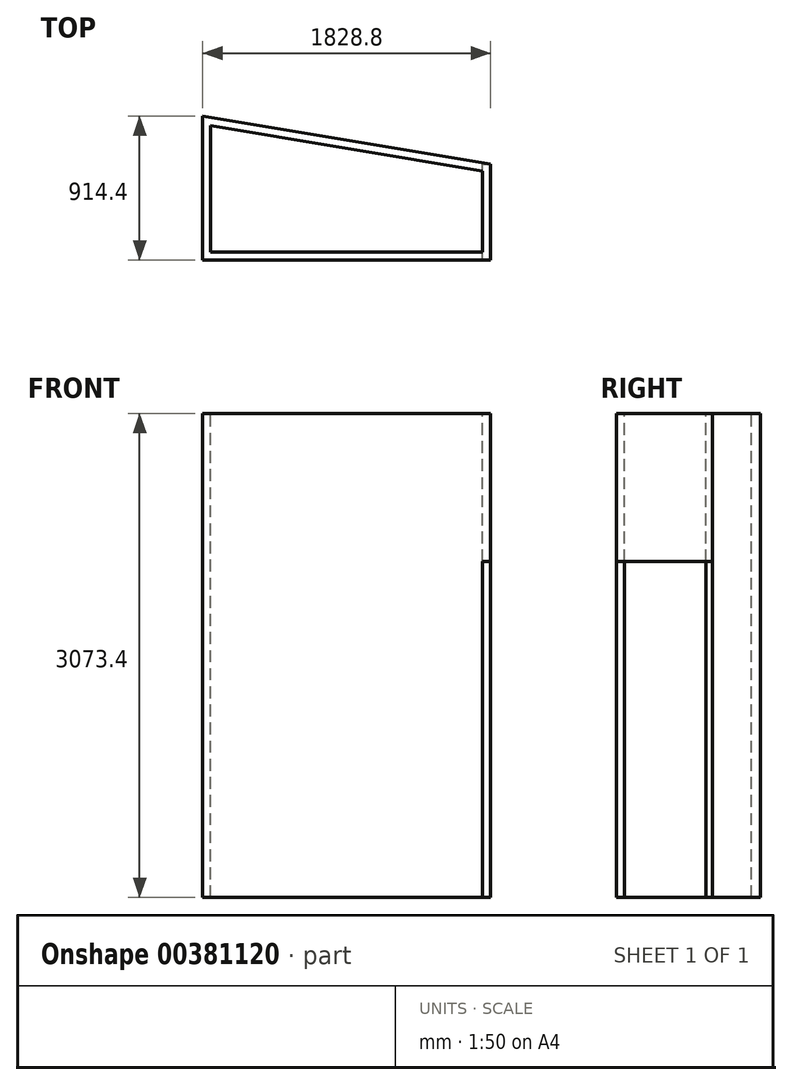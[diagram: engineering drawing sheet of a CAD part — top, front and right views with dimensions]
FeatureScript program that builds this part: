
annotation { "Feature Type Name" : "Feature", "Feature Type Description" : "" }
export const myFeature = defineFeature(function(context is Context, id is Id, definition is map)
    precondition{}
    {
        {
            var Q0;
            Q0=qCreatedBy(makeId("Top.planeOp"),FACE);
            var sketch = newSketch(context, id + "F0", { "sketchPlane" : qUnion([Q0])});
            skSolve(sketch);
        }
        {
            var Q0;
            Q0=qCreatedBy(makeId("Top.planeOp"),FACE);
            var sketch = newSketch(context, id + "F1", { "sketchPlane" : qUnion([Q0])});
            skLineSegment(sketch, "E0", {"start": v(-931.25, -130.48) * mm, "end": v(897.55, -130.48) * mm});
            skLineSegment(sketch, "E1", {"start": v(-931.25, -130.48) * mm, "end": v(-931.25, 783.92) * mm});
            skLineSegment(sketch, "E2", {"start": v(897.55, -130.48) * mm, "end": v(897.55, 479.12) * mm});
            skLineSegment(sketch, "E3", {"start": v(-931.25, 783.92) * mm, "end": v(897.55, 479.12) * mm});
            skSolve(sketch);
        }
        {
            var Q0;
            Q0=qSketchRegion(id+"F0",true);
            var Q1;
            Q1=makeQuery(id+"F1.imprint","IMPRINT",FACE,{"disambiguationData":[TD([[makeQuery(id+"F1.imprint","IMPRINT",EDGE,{"derivedFrom":sQuery(id+"F1.wireOp",EDGE,"E0")}),1.0]])]});
            extrude(context, id + "F2", {"entities" : qUnion([Q0, Q1]), "depth" : 25.4 * mm});
        }
        {
            var Q0;
            Q0=makeQuery(id+"F2.opExtrude","CAP_FACE",FACE,{"disambiguationData":[OSD([sQuery(id+"F1.wireOp",EDGE,"E0"),sQuery(id+"F1.wireOp",EDGE,"E1"),sQuery(id+"F1.wireOp",EDGE,"E2"),sQuery(id+"F1.wireOp",EDGE,"E3")])],"isStart":false});
            extrude(context, id + "F3", {"entities" : qUnion([Q0]), "operationType" : NewBodyOperationType.ADD, "depth" : 3048 * mm});
        }
        {
            var Q0;
            Q0=makeQuery(id+"F3.opExtrude","CAP_FACE",FACE,{"disambiguationData":[OSD([sQuery(id+"F1.wireOp",EDGE,"E0"),sQuery(id+"F1.wireOp",EDGE,"E1"),sQuery(id+"F1.wireOp",EDGE,"E2"),sQuery(id+"F1.wireOp",EDGE,"E3")])],"isStart":false});
            var sketch = newSketch(context, id + "F4", { "sketchPlane" : qUnion([Q0])});
            skLineSegment(sketch, "E4.0", {"start": v(846.75, 436.1) * mm, "end": v(-880.45, 723.96) * mm});
            skLineSegment(sketch, "E4.1", {"start": v(846.75, -79.68) * mm, "end": v(846.75, 436.1) * mm});
            skLineSegment(sketch, "E4.2", {"start": v(-880.45, -79.68) * mm, "end": v(846.75, -79.68) * mm});
            skLineSegment(sketch, "E4.3", {"start": v(-880.45, 723.96) * mm, "end": v(-880.45, -79.68) * mm});
            skLineSegment(sketch, "E5.0", {"start": v(891.2, 473.74) * mm, "end": v(-924.9, 776.43) * mm});
            skLineSegment(sketch, "E5.1", {"start": v(891.2, -124.13) * mm, "end": v(891.2, 473.74) * mm});
            skLineSegment(sketch, "E5.2", {"start": v(-924.9, -124.13) * mm, "end": v(891.2, -124.13) * mm});
            skLineSegment(sketch, "E5.3", {"start": v(-924.9, 776.43) * mm, "end": v(-924.9, -124.13) * mm});
            skSolve(sketch);
        }
        {
            var Q0;
            Q0=makeQuery(id+"F4.imprint","IMPRINT",FACE,{"disambiguationData":[TD([[makeQuery(id+"F4.imprint","IMPRINT",EDGE,{"derivedFrom":sQuery(id+"F4.wireOp",EDGE,"E4.0")}),1.0]])]});
            extrude(context, id + "F5", {"entities" : qUnion([Q0]), "operationType" : NewBodyOperationType.REMOVE, "oppositeDirection" : true, "depth" : 3302 * mm});
        }
        {
            var Q0;
            {var subQ0=sQuery(id+"F1.wireOp",EDGE,"E2");Q0=makeQuery(id+"F3.boolean.opBoolean","MERGE",FACE,{"derivedFrom":[makeQuery(id+"F2.opExtrude","SWEPT_FACE",FACE,{"disambiguationData":[OSD([subQ0])]}),makeQuery(id+"F3.opExtrude","SWEPT_FACE",FACE,{"disambiguationData":[OSD([subQ0])]})]});}
            var sketch = newSketch(context, id + "F6", { "sketchPlane" : qUnion([Q0])});
            skLineSegment(sketch, "E6.bottom", {"start": v(-130.48, 0) * mm, "end": v(479.12, 0) * mm});
            skLineSegment(sketch, "E6.top", {"start": v(-130.48, 2133.6) * mm, "end": v(479.12, 2133.6) * mm});
            skLineSegment(sketch, "E6.left", {"start": v(-130.48, 0) * mm, "end": v(-130.48, 2133.6) * mm});
            skLineSegment(sketch, "E6.right", {"start": v(479.12, 0) * mm, "end": v(479.12, 2133.6) * mm});
            skSolve(sketch);
        }
        {
            var Q0;
            Q0=makeQuery(id+"F6.imprint","IMPRINT",FACE,{"disambiguationData":[TD([[makeQuery(id+"F6.imprint","IMPRINT",EDGE,{"derivedFrom":sQuery(id+"F6.wireOp",EDGE,"E6.bottom")}),1.0]])]});
            extrude(context, id + "F7", {"entities" : qUnion([Q0]), "operationType" : NewBodyOperationType.REMOVE, "oppositeDirection" : true, "depth" : 50.8 * mm});
        }
    });
